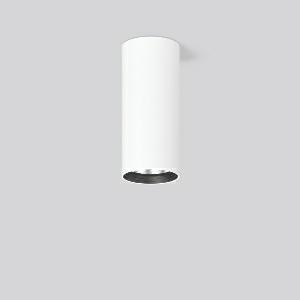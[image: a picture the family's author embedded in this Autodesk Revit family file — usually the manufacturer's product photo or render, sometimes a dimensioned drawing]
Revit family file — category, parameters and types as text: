
# Revit family: heledon_mini_a_931208_002_3_335b
name_source: partatom
category: Lighting Fixtures
units: mm (PartAtom-declared; Revit-internal decimal feet)

## family parameters
Cut with Voids When Loaded = No
Host = Face
Light Source = No
Part Type = Normal
Room Calculation Point = No
Round Connector Dimension = Use Diameter
Shared = No

## types (1)
- HELEDON mini A (1 x LED Modul 935, 3700 lm, 3500)
    Apparent Load = 29 VA
    Approval mark = CE
    CIE Flux Codes = 100 100 100 100 100
    Color Rendering = 92
    Color Temperature = 3500
    Default Elevation = 1800 mm
    Description = Series: HELEDON mini
Cylindrical surface-mounted downlight. Housing: die-cast aluminium, powder-coated. Internal ceiling frame polycarbonate with bayonet mounting. Black plastic ring and recessed LED to prevent glare from the side. Optical assembly with reflector made of MIRO-Silver with 98% total light reflection for outstanding efficiency - can be changed without tools. Best colour rendering index Ra>90. Suitable for Ceiling mounting. Easy installation with a separate ceiling frame with bayonet mounting and plug connection. Driver integrated. Connected via plug-in connector. High quality converter without flickering and stroboscopic effect. The following accessories can be mounted without use of tools: interchangeable lenses, decorative glasses, honeycomb louvre, clear and frosted diffusers, white interchangeable plastic ring. 
Colour: traffic white, matt (RAL 9016)
Diameter: 87 mm
Height: 197 mm
Lamp: LED
Socket: without socket
Colour temperature: 3500K
Colour rendering index (CRI): 92
System power: 29 W
Rated luminous flux: 3700 lm
Luminous efficiency: 128 lm/W
Control gear: Regulated power supply
Protection class: I
Type of protection: IP 20
    Height = 197 mm
    Lamp = 1 x LED Modul 935
    Lamp Light Flux = 3700 lm
    Lamp count = 1
    Length = 87 mm
    Lifetime = 50000 h
    Luminous efficacy = 128 lm/W
    Manufacturer = RZB
    ModVariant = No
    Model = 931208.002.3
    Mounting Place = Ceiling
    Mounting Type = Surface mounted
    Number of Poles = 1
    OnlyDefault = Yes
    Power Factor = 1
    Product Name = HELEDON mini A
    Product group = Surface mounted downlights
    ProductGroupID = 302
    Protection Class = Protection class I
    Protection Degree = IP 20
    RLX_Detail_Level = 1
    RLX_Emergency_Light_Flux = 0 lm
    RLX_Emergency_Type = 0
    RLX_Emergency_Type_DB = No
    RlxData = <blob elided: 106909 chars, md5=05959378>
    Socket = socket
    Standby Power = 0 W
    System Light Flux = 3700 lm
    System Power = 29 W
    Type Comments = Product without accessories
    Type Image = 931188.002.jpg
    URL = http://relux.com
    VarID = ---
    Voltage = 230 V
    Voltage Range = 220-240 V
    Weight = 0.00 kg
    Width = 0 mm  [stored 0 ft]

note: [stored X ft] marks values corroborated as IEEE doubles in the binary element streams (Revit-internal decimal feet)

## geometry (parser evidence)
native form markers: Blend x4, Sweep x9
no freeform markers — native parametric forms only
